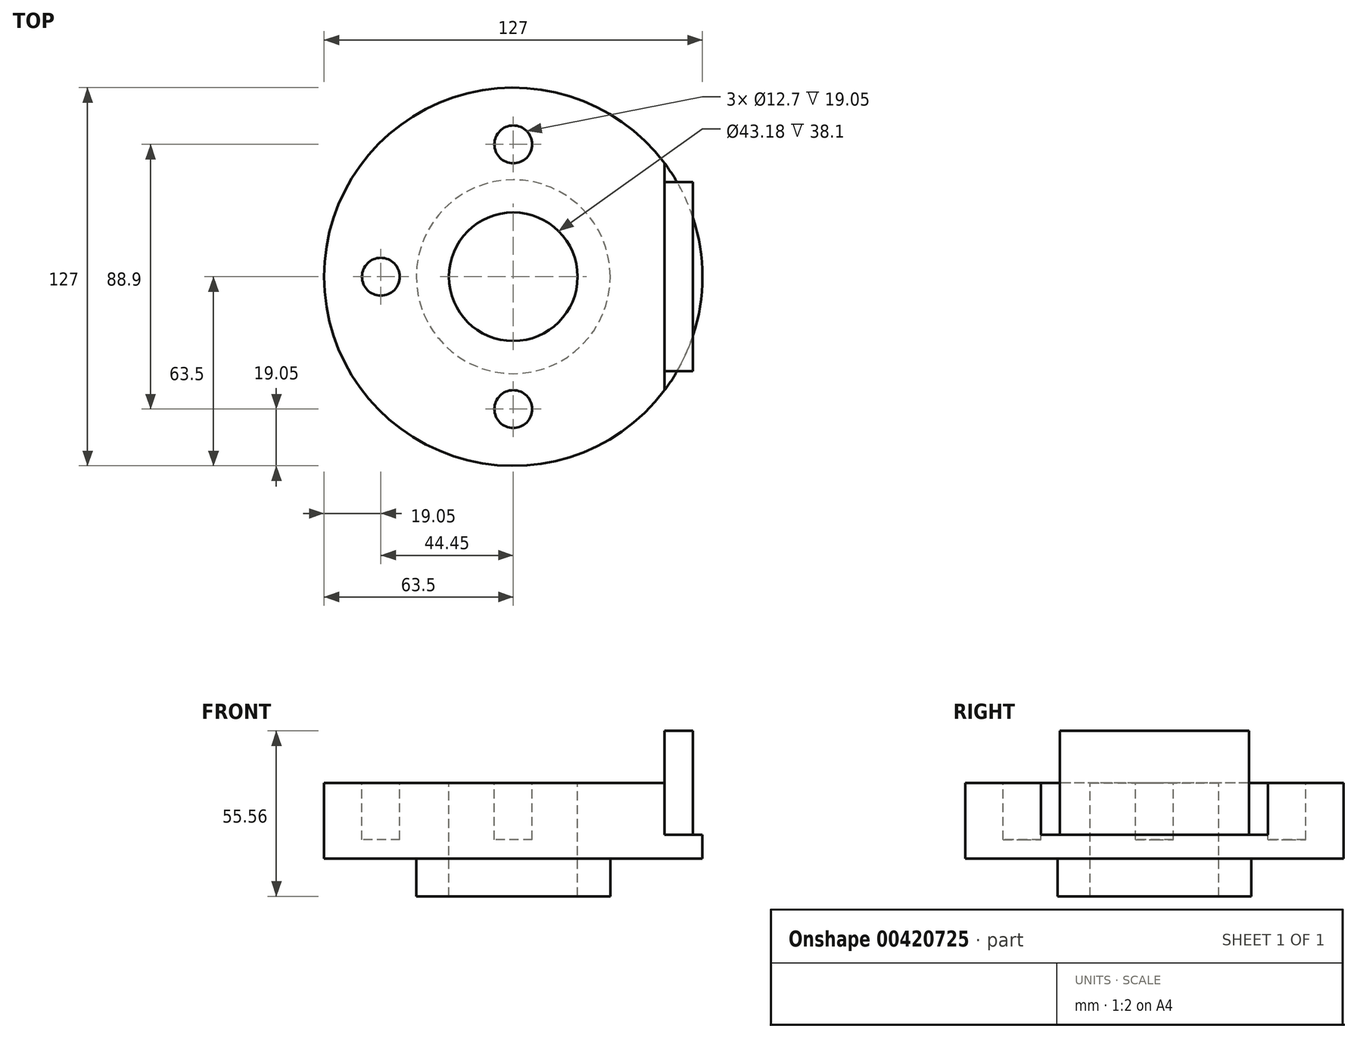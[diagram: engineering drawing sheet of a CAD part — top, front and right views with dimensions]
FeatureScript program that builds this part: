
annotation { "Feature Type Name" : "Feature", "Feature Type Description" : "" }
export const myFeature = defineFeature(function(context is Context, id is Id, definition is map)
    precondition{}
    {
        {
            var Q0;
            Q0=qCreatedBy(makeId("Top.planeOp"),FACE);
            var sketch = newSketch(context, id + "F0", { "sketchPlane" : qUnion([Q0])});
            skCircle(sketch, "E0", {"center": v(0, 0) * mm, "radius": 63.5 * mm});
            skSolve(sketch);
        }
        {
            var Q0;
            Q0=makeQuery(id+"F0.imprint","IMPRINT",FACE,{"disambiguationData":[TD([[makeQuery(id+"F0.imprint","IMPRINT",EDGE,{"derivedFrom":sQuery(id+"F0.wireOp",EDGE,"E0")}),1.0]])]});
            extrude(context, id + "F1", {"entities" : qUnion([Q0]), "depth" : 25.4 * mm});
        }
        {
            var Q0;
            Q0=makeQuery(id+"F1.opExtrude","CAP_FACE",FACE,{"disambiguationData":[OSD([sQuery(id+"F0.wireOp",EDGE,"E0")])],"isStart":false});
            var sketch = newSketch(context, id + "F2", { "sketchPlane" : qUnion([Q0])});
            skLineSegment(sketch, "E1", {"start": v(50.8, 38.1) * mm, "end": v(50.8, -38.1) * mm});
            skArc(sketch, "E2", {"start": v(50.8, -38.1) * mm, "mid": v(63.5, 0) * mm, "end": v(50.8, 38.1) * mm});
            skSolve(sketch);
        }
        {
            var Q0;
            Q0 = qSketchRegion(id + "F2", true);
            extrude(context, id + "F3", {"entities" : qUnion([Q0]), "operationType" : NewBodyOperationType.REMOVE, "oppositeDirection" : true, "depth" : 17.46 * mm});
        }
        {
            var Q0;
            Q0=makeQuery(id+"F1.opExtrude","CAP_FACE",FACE,{"disambiguationData":[OSD([sQuery(id+"F0.wireOp",EDGE,"E0")])],"isStart":false});
            var sketch = newSketch(context, id + "F4", { "sketchPlane" : qUnion([Q0])});
            skCircle(sketch, "E3", {"center": v(0, 0) * mm, "radius": 44.45 * mm, "construction": true});
            skCircle(sketch, "E4", {"center": v(0, 44.45) * mm, "radius": 6.35 * mm});
            skCircle(sketch, "E5", {"center": v(-44.45, 0) * mm, "radius": 6.35 * mm});
            skCircle(sketch, "E6", {"center": v(0, -44.45) * mm, "radius": 6.35 * mm});
            skSolve(sketch);
        }
        {
            var Q0;
            Q0 = qSketchRegion(id + "F4", true);
            extrude(context, id + "F5", {"entities" : qUnion([Q0]), "operationType" : NewBodyOperationType.REMOVE, "oppositeDirection" : true, "depth" : 19.05 * mm});
        }
        {
            var Q0;
            Q0=makeQuery(id+"F1.opExtrude","CAP_FACE",FACE,{"disambiguationData":[OSD([sQuery(id+"F0.wireOp",EDGE,"E0")])],"isStart":false});
            var sketch = newSketch(context, id + "F6", { "sketchPlane" : qUnion([Q0])});
            skCircle(sketch, "E7", {"center": v(0, 0) * mm, "radius": 21.59 * mm});
            skSolve(sketch);
        }
        {
            var Q0;
            Q0 = qSketchRegion(id + "F6", true);
            extrude(context, id + "F7", {"entities" : qUnion([Q0]), "operationType" : NewBodyOperationType.REMOVE, "endBound" : BoundingType.UP_TO_NEXT, "oppositeDirection" : true, "depth" : 25.4 * mm});
        }
        {
            var Q0;
            Q0=makeQuery(id+"F1.opExtrude","CAP_FACE",FACE,{"disambiguationData":[OSD([sQuery(id+"F0.wireOp",EDGE,"E0")])],"isStart":true});
            var sketch = newSketch(context, id + "F8", { "sketchPlane" : qUnion([Q0])});
            skCircle(sketch, "E8", {"center": v(0, 0) * mm, "radius": 32.54 * mm});
            skCircle(sketch, "E9", {"center": v(0, 0) * mm, "radius": 21.59 * mm});
            skSolve(sketch);
        }
        {
            var Q0;
            Q0 = qSketchRegion(id + "F8", true);
            extrude(context, id + "F9", {"entities" : qUnion([Q0]), "operationType" : NewBodyOperationType.ADD, "depth" : 12.7 * mm});
        }
        {
            var Q0;
            Q0=makeQuery(id+"F3.boolean.opBoolean","COPY",FACE,{"derivedFrom":makeQuery(id+"F3.opExtrude","SWEPT_FACE",FACE,{"disambiguationData":[OSD([sQuery(id+"F2.wireOp",EDGE,"E1")])]})});
            var sketch = newSketch(context, id + "F10", { "sketchPlane" : qUnion([Q0])});
            skLineSegment(sketch, "E10.bottom", {"start": v(0, 7.94) * mm, "end": v(31.75, 7.94) * mm});
            skLineSegment(sketch, "E11", {"start": v(0, 7.94) * mm, "end": v(0, 42.86) * mm, "construction": true});
            skPoint(sketch, "E11.endSnap0", {"position": v(0, 25.4) * mm});
            skLineSegment(sketch, "E12", {"start": v(0, 42.86) * mm, "end": v(31.75, 42.86) * mm});
            skLineSegment(sketch, "E13", {"start": v(31.75, 42.86) * mm, "end": v(31.75, 7.94) * mm});
            skLineSegment(sketch, "E14.MirrorCS", {"start": v(0, 42.86) * mm, "end": v(-31.75, 42.86) * mm});
            skLineSegment(sketch, "E15.MirrorCS", {"start": v(-31.75, 42.86) * mm, "end": v(-31.75, 7.94) * mm});
            skLineSegment(sketch, "E16.MirrorCS", {"start": v(0, 7.94) * mm, "end": v(-31.75, 7.94) * mm});
            skSolve(sketch);
        }
        {
            var Q0;
            Q0 = qSketchRegion(id + "F10", true);
            extrude(context, id + "F11", {"entities" : qUnion([Q0]), "operationType" : NewBodyOperationType.ADD, "depth" : 9.52 * mm});
        }
    });
